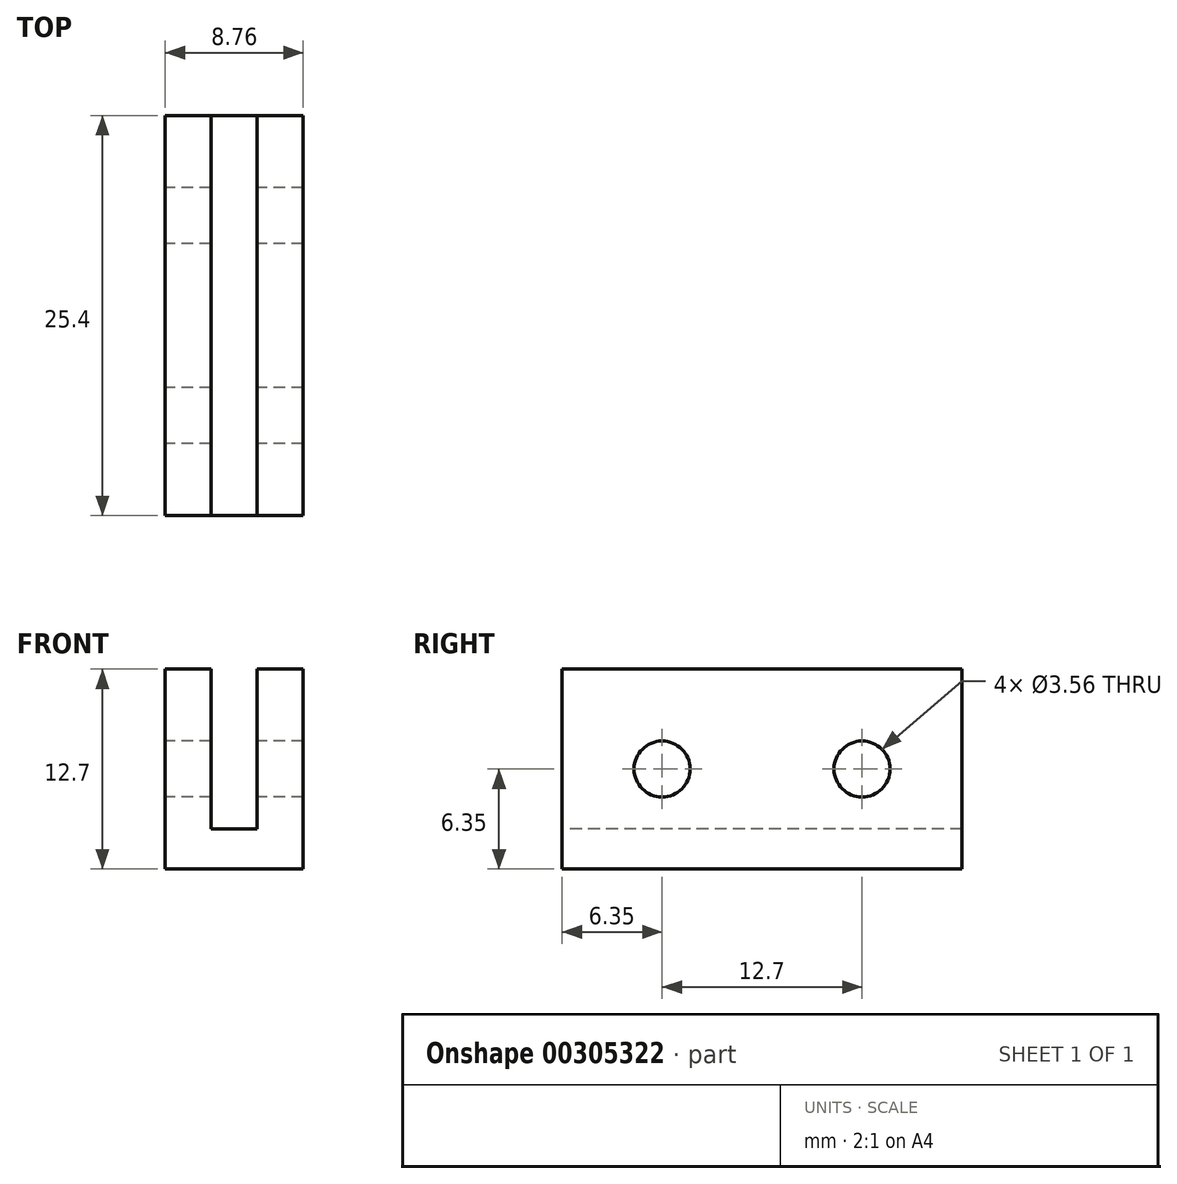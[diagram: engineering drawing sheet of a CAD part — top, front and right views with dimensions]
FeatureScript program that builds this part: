
annotation { "Feature Type Name" : "Feature", "Feature Type Description" : "" }
export const myFeature = defineFeature(function(context is Context, id is Id, definition is map)
    precondition{}
    {
        {
            var Q0;
            Q0=qCreatedBy(makeId("Top.planeOp"),FACE);
            var sketch = newSketch(context, id + "F0", { "sketchPlane" : qUnion([Q0])});
            skLineSegment(sketch, "E0.bottom", {"start": v(-1.46, 12.7) * mm, "end": v(1.46, 12.7) * mm});
            skLineSegment(sketch, "E0.top", {"start": v(-1.46, -12.7) * mm, "end": v(1.46, -12.7) * mm});
            skLineSegment(sketch, "E0.left", {"start": v(-1.46, 12.7) * mm, "end": v(-1.46, -12.7) * mm});
            skLineSegment(sketch, "E0.right", {"start": v(1.46, 12.7) * mm, "end": v(1.46, -12.7) * mm});
            skPoint(sketch, "E0.middle", {"position": v(0, 0) * mm});
            skLineSegment(sketch, "E1.bottom", {"start": v(-1.46, 12.7) * mm, "end": v(-4.38, 12.7) * mm});
            skLineSegment(sketch, "E1.top", {"start": v(-1.46, -12.7) * mm, "end": v(-4.38, -12.7) * mm});
            skLineSegment(sketch, "E1.right", {"start": v(-4.38, 12.7) * mm, "end": v(-4.38, -12.7) * mm});
            skLineSegment(sketch, "E2.bottom", {"start": v(1.46, 12.7) * mm, "end": v(4.38, 12.7) * mm});
            skLineSegment(sketch, "E2.top", {"start": v(1.46, -12.7) * mm, "end": v(4.38, -12.7) * mm});
            skLineSegment(sketch, "E2.right", {"start": v(4.38, 12.7) * mm, "end": v(4.38, -12.7) * mm});
            skSolve(sketch);
        }
        {
            var Q0;
            Q0 = qSketchRegion(id + "F0", true);
            extrude(context, id + "F1", {"entities" : qUnion([Q0]), "depth" : 2.54 * mm});
        }
        {
            var Q0;
            Q0=makeQuery(id+"F1.opExtrude","CAP_FACE",FACE,{"disambiguationData":[OSD([sQuery(id+"F0.wireOp",EDGE,"E0.bottom"),sQuery(id+"F0.wireOp",EDGE,"E0.top"),sQuery(id+"F0.wireOp",EDGE,"E1.bottom"),sQuery(id+"F0.wireOp",EDGE,"E1.top"),sQuery(id+"F0.wireOp",EDGE,"E1.right"),sQuery(id+"F0.wireOp",EDGE,"E2.bottom"),sQuery(id+"F0.wireOp",EDGE,"E2.top"),sQuery(id+"F0.wireOp",EDGE,"E2.right")])],"isStart":false});
            var sketch = newSketch(context, id + "F2", { "sketchPlane" : qUnion([Q0])});
            skLineSegment(sketch, "E3.bottom", {"start": v(-4.38, 12.7) * mm, "end": v(-1.46, 12.7) * mm});
            skLineSegment(sketch, "E3.top", {"start": v(-4.38, -12.7) * mm, "end": v(-1.46, -12.7) * mm});
            skLineSegment(sketch, "E3.left", {"start": v(-4.38, 12.7) * mm, "end": v(-4.38, -12.7) * mm});
            skLineSegment(sketch, "E3.right", {"start": v(-1.46, 12.7) * mm, "end": v(-1.46, -12.7) * mm});
            skLineSegment(sketch, "E4.bottom", {"start": v(4.38, 12.7) * mm, "end": v(1.46, 12.7) * mm});
            skLineSegment(sketch, "E4.top", {"start": v(4.38, -12.7) * mm, "end": v(1.46, -12.7) * mm});
            skLineSegment(sketch, "E4.left", {"start": v(4.38, 12.7) * mm, "end": v(4.38, -12.7) * mm});
            skLineSegment(sketch, "E4.right", {"start": v(1.46, 12.7) * mm, "end": v(1.46, -12.7) * mm});
            skSolve(sketch);
        }
        {
            var Q0;
            Q0 = qSketchRegion(id + "F2", true);
            extrude(context, id + "F3", {"entities" : qUnion([Q0]), "operationType" : NewBodyOperationType.ADD, "depth" : 10.16 * mm});
        }
        {
            var Q0;
            Q0=makeQuery(id+"F3.boolean.opBoolean","MERGE",FACE,{"derivedFrom":[makeQuery(id+"F1.opExtrude","SWEPT_FACE",FACE,{"disambiguationData":[OSD([sQuery(id+"F0.wireOp",EDGE,"E1.right")])]}),makeQuery(id+"F3.opExtrude","SWEPT_FACE",FACE,{"disambiguationData":[OSD([sQuery(id+"F2.wireOp",EDGE,"E3.left")])]})]});
            var sketch = newSketch(context, id + "F4", { "sketchPlane" : qUnion([Q0])});
            skPoint(sketch, "E5.orphan", {"position": v(0, 12.7) * mm});
            skPoint(sketch, "E6.orphan", {"position": v(12.7, 6.35) * mm});
            skCircle(sketch, "E7", {"center": v(-6.35, 6.35) * mm, "radius": 1.78 * mm});
            skCircle(sketch, "E8", {"center": v(6.35, 6.35) * mm, "radius": 1.78 * mm});
            skPoint(sketch, "E9.orphan", {"position": v(-12.7, 6.35) * mm});
            skPoint(sketch, "E10.orphan", {"position": v(0, 6.35) * mm});
            skSolve(sketch);
        }
        {
            var Q0;
            Q0 = qSketchRegion(id + "F4", true);
            extrude(context, id + "F5", {"entities" : qUnion([Q0]), "operationType" : NewBodyOperationType.REMOVE, "oppositeDirection" : true, "depth" : 25.4 * mm});
        }
    });
